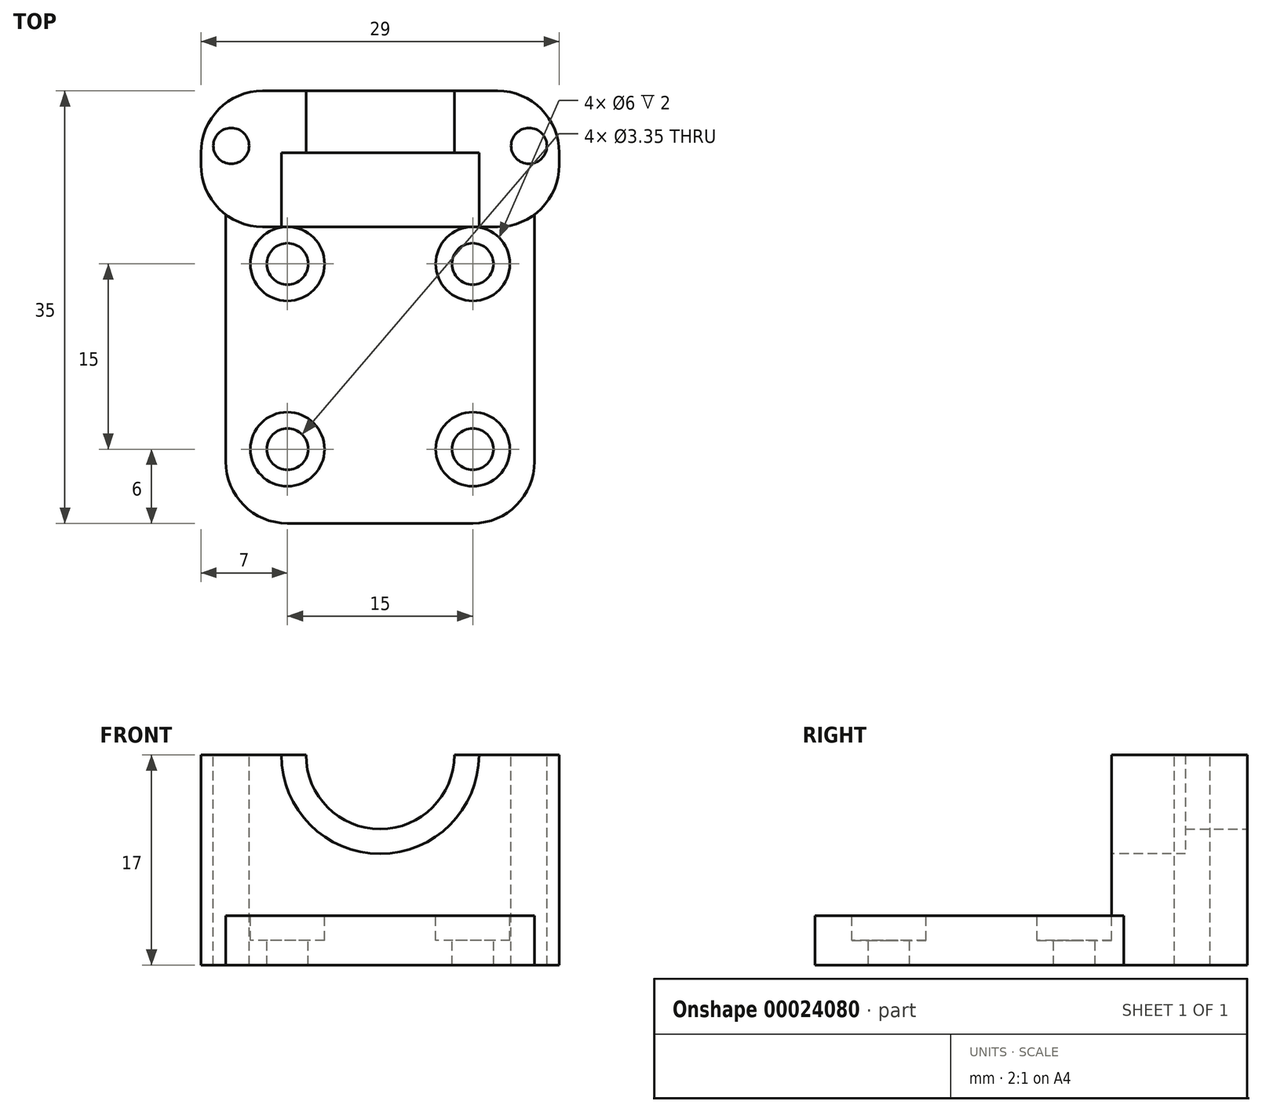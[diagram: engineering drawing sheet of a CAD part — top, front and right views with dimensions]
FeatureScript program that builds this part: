
annotation { "Feature Type Name" : "Feature", "Feature Type Description" : "" }
export const myFeature = defineFeature(function(context is Context, id is Id, definition is map)
    precondition{}
    {
        {
            var Q0;
            Q0=qCreatedBy(makeId("Top.planeOp"),FACE);
            var sketch = newSketch(context, id + "F0", { "sketchPlane" : qUnion([Q0])});
            skLineSegment(sketch, "E0.bottom", {"start": v(0, 0) * mm, "end": v(25, 0) * mm});
            skLineSegment(sketch, "E0.top", {"start": v(0, 35) * mm, "end": v(25, 35) * mm});
            skLineSegment(sketch, "E0.left", {"start": v(0, 0) * mm, "end": v(0, 35) * mm});
            skLineSegment(sketch, "E0.right", {"start": v(25, 0) * mm, "end": v(25, 35) * mm});
            skSolve(sketch);
        }
        {
            var Q0;
            Q0=qSketchRegion(id+"F0",true);
            extrude(context, id + "F1", {"entities" : qUnion([Q0]), "depth" : 4 * mm});
        }
        {
            var Q0;
            Q0=makeQuery(id+"F1.opExtrude","CAP_FACE",FACE,{"disambiguationData":[OSD([sQuery(id+"F0.wireOp",EDGE,"E0.bottom"),sQuery(id+"F0.wireOp",EDGE,"E0.top"),sQuery(id+"F0.wireOp",EDGE,"E0.left"),sQuery(id+"F0.wireOp",EDGE,"E0.right")])],"isStart":false});
            var sketch = newSketch(context, id + "F2", { "sketchPlane" : qUnion([Q0])});
            skCircle(sketch, "E1", {"center": v(5, 21) * mm, "radius": 1.68 * mm});
            skCircle(sketch, "E2", {"center": v(20, 21) * mm, "radius": 1.68 * mm});
            skCircle(sketch, "E3", {"center": v(5, 6) * mm, "radius": 1.68 * mm});
            skCircle(sketch, "E4", {"center": v(20, 6) * mm, "radius": 1.68 * mm});
            skLineSegment(sketch, "E5", {"start": v(5, 21) * mm, "end": v(0, 21) * mm});
            skLineSegment(sketch, "E6", {"start": v(20, 6) * mm, "end": v(25, 6) * mm});
            skCircle(sketch, "E7", {"center": v(5, 21) * mm, "radius": 3 * mm});
            skCircle(sketch, "E8", {"center": v(20, 21) * mm, "radius": 3 * mm});
            skCircle(sketch, "E9", {"center": v(5, 6) * mm, "radius": 3 * mm});
            skCircle(sketch, "E10", {"center": v(20, 6) * mm, "radius": 3 * mm});
            skLineSegment(sketch, "E11", {"start": v(5, 6) * mm, "end": v(5, 0) * mm});
            skSolve(sketch);
        }
        {
            var Q0;
            Q0=makeQuery(id+"F1.opExtrude","CAP_FACE",FACE,{"disambiguationData":[OSD([sQuery(id+"F0.wireOp",EDGE,"E0.bottom"),sQuery(id+"F0.wireOp",EDGE,"E0.top"),sQuery(id+"F0.wireOp",EDGE,"E0.left"),sQuery(id+"F0.wireOp",EDGE,"E0.right")])],"isStart":false});
            var sketch = newSketch(context, id + "F3", { "sketchPlane" : qUnion([Q0])});
            skLineSegment(sketch, "E12.bottom", {"start": v(0, 35) * mm, "end": v(25, 35) * mm});
            skLineSegment(sketch, "E12.top", {"start": v(0, 24) * mm, "end": v(25, 24) * mm});
            skLineSegment(sketch, "E12.left", {"start": v(0, 35) * mm, "end": v(0, 24) * mm});
            skLineSegment(sketch, "E12.right", {"start": v(25, 35) * mm, "end": v(25, 24) * mm});
            skSolve(sketch);
        }
        {
            var Q0;
            Q0=qSketchRegion(id+"F3",true);
            extrude(context, id + "F4", {"entities" : qUnion([Q0]), "operationType" : NewBodyOperationType.ADD, "depth" : 13 * mm});
        }
        {
            var Q0;
            Q0=makeQuery(id+"F4.boolean.opBoolean","MERGE",FACE,{"derivedFrom":[makeQuery(id+"F1.opExtrude","SWEPT_FACE",FACE,{"disambiguationData":[OSD([sQuery(id+"F0.wireOp",EDGE,"E0.top")])]}),makeQuery(id+"F4.opExtrude","SWEPT_FACE",FACE,{"disambiguationData":[OSD([sQuery(id+"F3.wireOp",EDGE,"E12.bottom")])]})]});
            var sketch = newSketch(context, id + "F5", { "sketchPlane" : qUnion([Q0])});
            skCircle(sketch, "E13", {"center": v(-12.5, 17) * mm, "radius": 6 * mm});
            skSolve(sketch);
        }
        {
            var Q0;
            {var subQ0=makeQuery(id+"F4.opExtrude","CAP_EDGE",EDGE,{"disambiguationData":[OSD([sQuery(id+"F3.wireOp",EDGE,"E12.bottom")])],"isStart":false});var subQ1=sQuery(id+"F5.wireOp",EDGE,"E13");var subQ3=makeQuery(id+"F5.imprint","INTERSECT",VERTEX,{"disambiguationData":[OD(0.0)],"derivedFrom":[subQ0,subQ1]});Q0=makeQuery(id+"F5.imprint","IMPRINT",FACE,{"disambiguationData":[TD([[makeQuery(id+"F5.imprint","IMPRINT",EDGE,{"disambiguationData":[TD([[subQ3,1.0]])],"derivedFrom":subQ1}),1.0]])]});}
            extrude(context, id + "F6", {"entities" : qUnion([Q0]), "operationType" : NewBodyOperationType.REMOVE, "oppositeDirection" : true, "depth" : 6 * mm});
        }
        {
            var Q0;
            Q0=makeQuery(id+"F4.opExtrude","SWEPT_FACE",FACE,{"disambiguationData":[OSD([sQuery(id+"F3.wireOp",EDGE,"E12.top")])]});
            var sketch = newSketch(context, id + "F7", { "sketchPlane" : qUnion([Q0])});
            skCircle(sketch, "E14", {"center": v(12.5, 17) * mm, "radius": 8 * mm});
            skSolve(sketch);
        }
        {
            var Q0;
            Q0=qSketchRegion(id+"F7",true);
            extrude(context, id + "F8", {"entities" : qUnion([Q0]), "operationType" : NewBodyOperationType.REMOVE, "oppositeDirection" : true, "depth" : 6 * mm});
        }
        {
            var Q0;
            Q0=makeQuery(id+"F2.imprint","IMPRINT",FACE,{"disambiguationData":[TD([[makeQuery(id+"F2.imprint","IMPRINT",EDGE,{"derivedFrom":sQuery(id+"F2.wireOp",EDGE,"E1")}),-1.0]])]});
            var Q1;
            Q1=makeQuery(id+"F2.imprint","IMPRINT",FACE,{"disambiguationData":[TD([[makeQuery(id+"F2.imprint","IMPRINT",EDGE,{"derivedFrom":sQuery(id+"F2.wireOp",EDGE,"E2")}),-1.0]])]});
            var Q2;
            Q2=makeQuery(id+"F2.imprint","IMPRINT",FACE,{"disambiguationData":[TD([[makeQuery(id+"F2.imprint","IMPRINT",EDGE,{"derivedFrom":sQuery(id+"F2.wireOp",EDGE,"E4")}),-1.0]])]});
            var Q3;
            Q3=makeQuery(id+"F2.imprint","IMPRINT",FACE,{"disambiguationData":[TD([[makeQuery(id+"F2.imprint","IMPRINT",EDGE,{"derivedFrom":sQuery(id+"F2.wireOp",EDGE,"E3")}),-1.0]])]});
            extrude(context, id + "F9", {"entities" : qUnion([Q0, Q1, Q2, Q3]), "operationType" : NewBodyOperationType.REMOVE, "oppositeDirection" : true, "depth" : 2 * mm});
        }
        {
            var Q0;
            Q0=makeQuery(id+"F1.opExtrude","SWEPT_EDGE",EDGE,{"disambiguationData":[OSD([sQuery(id+"F0.wireOp",EDGE,"E0.bottom"),sQuery(id+"F0.wireOp",EDGE,"E0.left")])]});
            var Q1;
            Q1=makeQuery(id+"F1.opExtrude","SWEPT_EDGE",EDGE,{"disambiguationData":[OSD([sQuery(id+"F0.wireOp",EDGE,"E0.bottom"),sQuery(id+"F0.wireOp",EDGE,"E0.right")])]});
            fillet(context, id + "F10", {"entities" : qUnion([Q0, Q1]), "radius" : 5 * mm, "tangentPropagation" : true, "allowEdgeOverflow" : false});
        }
        {
            var Q0;
            Q0=makeQuery(id+"F4.boolean.opBoolean","MERGE",FACE,{"derivedFrom":[makeQuery(id+"F1.opExtrude","SWEPT_FACE",FACE,{"disambiguationData":[OSD([sQuery(id+"F0.wireOp",EDGE,"E0.left")])]}),makeQuery(id+"F4.opExtrude","SWEPT_FACE",FACE,{"disambiguationData":[OSD([sQuery(id+"F3.wireOp",EDGE,"E12.left")])]})]});
            var sketch = newSketch(context, id + "F11", { "sketchPlane" : qUnion([Q0])});
            skLineSegment(sketch, "E15.bottom", {"start": v(-35, 0) * mm, "end": v(-24, 0) * mm});
            skLineSegment(sketch, "E15.top", {"start": v(-35, 17) * mm, "end": v(-24, 17) * mm});
            skLineSegment(sketch, "E15.left", {"start": v(-35, 0) * mm, "end": v(-35, 17) * mm});
            skLineSegment(sketch, "E15.right", {"start": v(-24, 0) * mm, "end": v(-24, 17) * mm});
            skSolve(sketch);
        }
        {
            var Q0;
            Q0=qSketchRegion(id+"F11",true);
            extrude(context, id + "F12", {"entities" : qUnion([Q0]), "operationType" : NewBodyOperationType.ADD, "depth" : 2 * mm});
        }
        {
            var Q0;
            Q0=makeQuery(id+"F4.boolean.opBoolean","MERGE",FACE,{"derivedFrom":[makeQuery(id+"F1.opExtrude","SWEPT_FACE",FACE,{"disambiguationData":[OSD([sQuery(id+"F0.wireOp",EDGE,"E0.right")])]}),makeQuery(id+"F4.opExtrude","SWEPT_FACE",FACE,{"disambiguationData":[OSD([sQuery(id+"F3.wireOp",EDGE,"E12.right")])]})]});
            var sketch = newSketch(context, id + "F13", { "sketchPlane" : qUnion([Q0])});
            skLineSegment(sketch, "E16.bottom", {"start": v(35, 0) * mm, "end": v(24, 0) * mm});
            skLineSegment(sketch, "E16.top", {"start": v(35, 17) * mm, "end": v(24, 17) * mm});
            skLineSegment(sketch, "E16.left", {"start": v(35, 0) * mm, "end": v(35, 17) * mm});
            skLineSegment(sketch, "E16.right", {"start": v(24, 0) * mm, "end": v(24, 17) * mm});
            skSolve(sketch);
        }
        {
            var Q0;
            Q0=qSketchRegion(id+"F13",true);
            extrude(context, id + "F14", {"entities" : qUnion([Q0]), "operationType" : NewBodyOperationType.ADD, "depth" : 2 * mm});
        }
        {
            var Q0;
            {var subQ0=sQuery(id+"F3.wireOp",EDGE,"E12.bottom");var subQ1=sQuery(id+"F3.wireOp",EDGE,"E12.top");var subQ2=sQuery(id+"F3.wireOp",EDGE,"E12.left");Q0=makeQuery(id+"F8.boolean.opBoolean","SPLIT",FACE,{"disambiguationData":[TD([makeQuery(id+"F1.opExtrude","SWEPT_FACE",FACE,{"disambiguationData":[OSD([sQuery(id+"F0.wireOp",EDGE,"E0.left")])]})])],"derivedFrom":makeQuery(id+"F4.opExtrude","CAP_FACE",FACE,{"disambiguationData":[OSD([subQ0,subQ1,subQ2,sQuery(id+"F3.wireOp",EDGE,"E12.right")])],"isStart":false})});}
            var sketch = newSketch(context, id + "F15", { "sketchPlane" : qUnion([Q0])});
            skCircle(sketch, "E17", {"center": v(0.45, 30.55) * mm, "radius": 1.45 * mm});
            skCircle(sketch, "E18", {"center": v(24.55, 30.55) * mm, "radius": 1.45 * mm});
            skSolve(sketch);
        }
        {
            var Q0;
            Q0=qSketchRegion(id+"F15",true);
            extrude(context, id + "F16", {"entities" : qUnion([Q0]), "operationType" : NewBodyOperationType.REMOVE, "oppositeDirection" : true, "depth" : 25 * mm});
        }
        {
            var Q0;
            Q0=makeQuery(id+"F12.opExtrude","CAP_EDGE",EDGE,{"disambiguationData":[OSD([sQuery(id+"F11.wireOp",EDGE,"E15.right")])],"isStart":false});
            var Q1;
            Q1=makeQuery(id+"F12.opExtrude","CAP_EDGE",EDGE,{"disambiguationData":[OSD([sQuery(id+"F11.wireOp",EDGE,"E15.left")])],"isStart":false});
            var Q2;
            Q2=makeQuery(id+"F14.opExtrude","CAP_EDGE",EDGE,{"disambiguationData":[OSD([sQuery(id+"F13.wireOp",EDGE,"E16.left")])],"isStart":false});
            var Q3;
            Q3=makeQuery(id+"F14.opExtrude","CAP_EDGE",EDGE,{"disambiguationData":[OSD([sQuery(id+"F13.wireOp",EDGE,"E16.right")])],"isStart":false});
            fillet(context, id + "F17", {"entities" : qUnion([Q0, Q1, Q2, Q3]), "radius" : 5 * mm, "tangentPropagation" : true, "allowEdgeOverflow" : false});
        }
        {
            var Q0;
            Q0=makeQuery(id+"F2.imprint","IMPRINT",FACE,{"disambiguationData":[TD([[makeQuery(id+"F2.imprint","IMPRINT",EDGE,{"derivedFrom":sQuery(id+"F2.wireOp",EDGE,"E1")}),1.0]])]});
            var Q1;
            Q1=makeQuery(id+"F2.imprint","IMPRINT",FACE,{"disambiguationData":[TD([[makeQuery(id+"F2.imprint","IMPRINT",EDGE,{"derivedFrom":sQuery(id+"F2.wireOp",EDGE,"E2")}),1.0]])]});
            var Q2;
            Q2=makeQuery(id+"F2.imprint","IMPRINT",FACE,{"disambiguationData":[TD([[makeQuery(id+"F2.imprint","IMPRINT",EDGE,{"derivedFrom":sQuery(id+"F2.wireOp",EDGE,"E4")}),1.0]])]});
            var Q3;
            Q3=makeQuery(id+"F2.imprint","IMPRINT",FACE,{"disambiguationData":[TD([[makeQuery(id+"F2.imprint","IMPRINT",EDGE,{"derivedFrom":sQuery(id+"F2.wireOp",EDGE,"E3")}),1.0]])]});
            extrude(context, id + "F18", {"entities" : qUnion([Q0, Q1, Q2, Q3]), "operationType" : NewBodyOperationType.REMOVE, "endBound" : BoundingType.SYMMETRIC, "oppositeDirection" : true, "depth" : 25 * mm});
        }
    });
